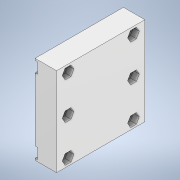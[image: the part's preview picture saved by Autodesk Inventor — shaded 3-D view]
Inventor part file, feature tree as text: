
AUTODESK INVENTOR PART (.ipt)
format: ipt  version: 2020 (Build 240168000, 168)  size: 200,192 bytes
history: native  units: mm
features: extrude x4, sketch x3, other x1
ambient origin geometry x8: Origin, YZ Plane, XZ Plane, XY Plane, X Axis, Y Axis, Z Axis, Center Point
bodies: Body1 (feature_tree)
feature tree (8):
  other  "Bryła1"
  extrude  "Wyciągnięcie proste1"  Depth=74.0mm
  sketch  "Szkic2"
  extrude  "Wyciągnięcie proste2"  Depth=74.0mm
  extrude  "Wyciągnięcie proste3"  Depth=18.0mm TaperAngle=0.0deg
  extrude  "Wyciągnięcie proste4"  Depth=6.0mm
  sketch  "Szkic1"
  sketch  "Szkic3"
